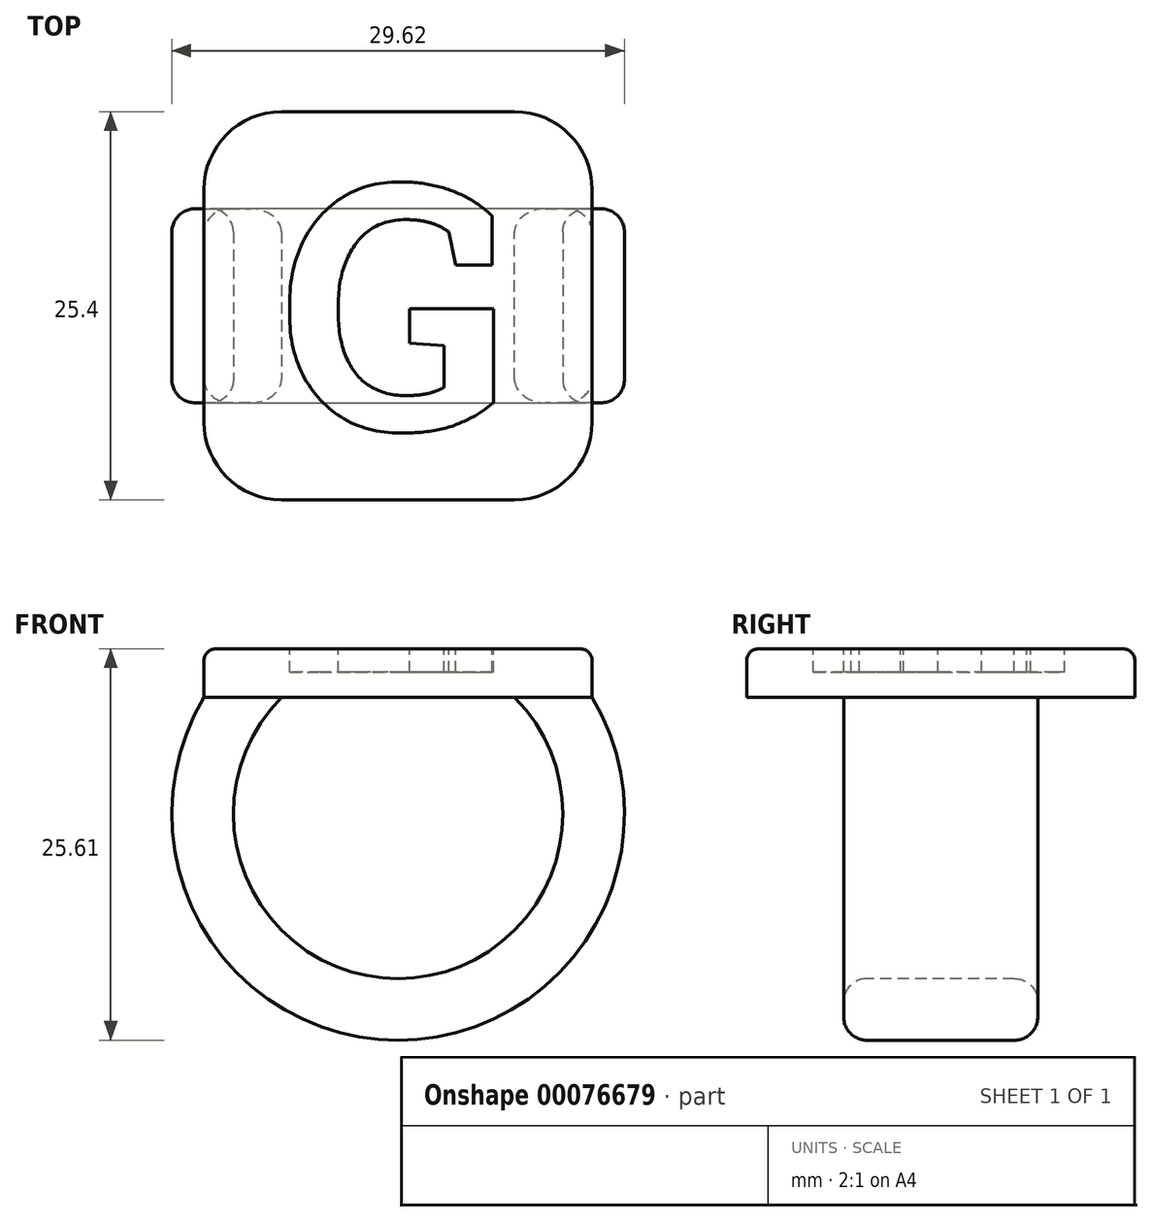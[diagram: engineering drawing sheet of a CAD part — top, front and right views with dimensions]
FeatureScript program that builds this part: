
annotation { "Feature Type Name" : "Feature", "Feature Type Description" : "" }
export const myFeature = defineFeature(function(context is Context, id is Id, definition is map)
    precondition{}
    {
        {
            var Q0;
            Q0=qCreatedBy(makeId("Top.planeOp"),FACE);
            var sketch = newSketch(context, id + "F0", { "sketchPlane" : qUnion([Q0])});
            skLineSegment(sketch, "E0.bottom", {"start": v(12.7, -12.7) * mm, "end": v(-12.7, -12.7) * mm});
            skLineSegment(sketch, "E0.top", {"start": v(12.7, 12.7) * mm, "end": v(-12.7, 12.7) * mm});
            skLineSegment(sketch, "E0.left", {"start": v(12.7, -12.7) * mm, "end": v(12.7, 12.7) * mm});
            skLineSegment(sketch, "E0.right", {"start": v(-12.7, -12.7) * mm, "end": v(-12.7, 12.7) * mm});
            skPoint(sketch, "E0.middle", {"position": v(0, 0) * mm});
            skSolve(sketch);
        }
        {
            var Q0;
            Q0 = qSketchRegion(id + "F0", true);
            extrude(context, id + "F1", {"entities" : qUnion([Q0]), "depth" : 3.17 * mm});
        }
        {
            var Q0;
            Q0=qCreatedBy(makeId("Front.planeOp"),FACE);
            var sketch = newSketch(context, id + "F2", { "sketchPlane" : qUnion([Q0])});
            skArc(sketch, "E1", {"start": v(-10.16, 0) * mm, "mid": v(0, -20.32) * mm, "end": v(10.16, 0) * mm});
            skSolve(sketch);
        }
        {
            var Q0;
            Q0=makeQuery(id+"F1.opExtrude","CAP_FACE",FACE,{"disambiguationData":[OSD([sQuery(id+"F0.wireOp",EDGE,"E0.bottom"),sQuery(id+"F0.wireOp",EDGE,"E0.top"),sQuery(id+"F0.wireOp",EDGE,"E0.left"),sQuery(id+"F0.wireOp",EDGE,"E0.right")])],"isStart":true});
            var sketch = newSketch(context, id + "F3", { "sketchPlane" : qUnion([Q0])});
            skLineSegment(sketch, "E2.bottom", {"start": v(-7.62, -6.35) * mm, "end": v(-12.7, -6.35) * mm});
            skLineSegment(sketch, "E2.top", {"start": v(-7.62, 6.35) * mm, "end": v(-12.7, 6.35) * mm});
            skLineSegment(sketch, "E2.left", {"start": v(-7.62, -6.35) * mm, "end": v(-7.62, 6.35) * mm});
            skLineSegment(sketch, "E2.right", {"start": v(-12.7, -6.35) * mm, "end": v(-12.7, 6.35) * mm});
            skPoint(sketch, "E2.middle", {"position": v(-10.16, 0) * mm});
            skSolve(sketch);
        }
        {
            var Q0;
            Q0 = qSketchRegion(id + "F3", true);
            var Q1;
            Q1 = qConstructionFilter(qBodyType(qCreatedBy(id + "F2" ,EDGE), BodyType.WIRE), ConstructionObject.NO);
            sweep(context, id + "F4", {"operationType" : NewBodyOperationType.ADD, "profiles" : qUnion([Q0]), "path" : qUnion([Q1])});
        }
        {
            var Q0;
            Q0=qCreatedBy(makeId("Front.planeOp"),FACE);
            var sketch = newSketch(context, id + "F5", { "sketchPlane" : qUnion([Q0])});
            skArc(sketch, "E3.0", {"start": v(9.45, -2.44) * mm, "mid": v(8.62, -1.15) * mm, "end": v(7.62, 0) * mm});
            skLineSegment(sketch, "E3.1", {"start": v(9.45, -2.44) * mm, "end": v(10.16, 0) * mm});
            skLineSegment(sketch, "E3.2", {"start": v(12.7, 0) * mm, "end": v(7.62, 0) * mm});
            skPoint(sketch, "E4.orphan", {"position": v(-7.62, 0) * mm});
            skLineSegment(sketch, "E5.trimOffspring", {"start": v(-7.62, 0) * mm, "end": v(-12.7, 0) * mm});
            skSolve(sketch);
        }
        {
            var Q0;
            Q0 = qSketchRegion(id + "F5", true);
            extrude(context, id + "F6", {"entities" : qUnion([Q0]), "operationType" : NewBodyOperationType.ADD, "depth" : 6.35 * mm, "hasSecondDirection" : true, "secondDirectionOppositeDirection" : true, "secondDirectionDepth" : 6.35 * mm});
        }
        {
            var Q0;
            Q0=makeQuery(id+"F1.opExtrude","SWEPT_EDGE",EDGE,{"disambiguationData":[OSD([sQuery(id+"F0.wireOp",EDGE,"E0.bottom"),sQuery(id+"F0.wireOp",EDGE,"E0.left")])]});
            var Q1;
            Q1=makeQuery(id+"F1.opExtrude","SWEPT_EDGE",EDGE,{"disambiguationData":[OSD([sQuery(id+"F0.wireOp",EDGE,"E0.top"),sQuery(id+"F0.wireOp",EDGE,"E0.left")])]});
            var Q2;
            Q2=makeQuery(id+"F1.opExtrude","SWEPT_EDGE",EDGE,{"disambiguationData":[OSD([sQuery(id+"F0.wireOp",EDGE,"E0.top"),sQuery(id+"F0.wireOp",EDGE,"E0.right")])]});
            var Q3;
            Q3=makeQuery(id+"F1.opExtrude","SWEPT_EDGE",EDGE,{"disambiguationData":[OSD([sQuery(id+"F0.wireOp",EDGE,"E0.bottom"),sQuery(id+"F0.wireOp",EDGE,"E0.right")])]});
            fillet(context, id + "F7", {"entities" : qUnion([Q0, Q1, Q2, Q3]), "radius" : 5.08 * mm, "tangentPropagation" : true, "allowEdgeOverflow" : false});
        }
        {
            var Q0;
            Q0=makeQuery(id+"F6.boolean.opBoolean","MERGE",EDGE,{"derivedFrom":[makeQuery(id+"F4.opSweep","SWEPT_EDGE",EDGE,{"disambiguationData":[OSD([sQuery(id+"F2.wireOp",EDGE,"E1"),sQuery(id+"F3.wireOp",EDGE,"E2.top"),sQuery(id+"F3.wireOp",EDGE,"E2.left")])]}),makeQuery(id+"F6.opExtrude","CAP_EDGE",EDGE,{"disambiguationData":[OSD([sQuery(id+"F5.wireOp",EDGE,"E3.0")])],"isStart":false})]});
            var Q1;
            Q1=makeQuery(id+"F4.opSweep","SWEPT_EDGE",EDGE,{"disambiguationData":[OSD([sQuery(id+"F0.wireOp",EDGE,"E0.right"),sQuery(id+"F2.wireOp",EDGE,"E1"),sQuery(id+"F3.wireOp",EDGE,"E2.top"),sQuery(id+"F3.wireOp",EDGE,"E2.right")])]});
            var Q2;
            Q2=makeQuery(id+"F4.opSweep","SWEPT_EDGE",EDGE,{"disambiguationData":[OSD([sQuery(id+"F0.wireOp",EDGE,"E0.right"),sQuery(id+"F2.wireOp",EDGE,"E1"),sQuery(id+"F3.wireOp",EDGE,"E2.bottom"),sQuery(id+"F3.wireOp",EDGE,"E2.right")])]});
            var Q3;
            Q3=makeQuery(id+"F6.boolean.opBoolean","MERGE",EDGE,{"derivedFrom":[makeQuery(id+"F4.opSweep","SWEPT_EDGE",EDGE,{"disambiguationData":[OSD([sQuery(id+"F2.wireOp",EDGE,"E1"),sQuery(id+"F3.wireOp",EDGE,"E2.bottom"),sQuery(id+"F3.wireOp",EDGE,"E2.left")])]}),makeQuery(id+"F6.opExtrude","CAP_EDGE",EDGE,{"disambiguationData":[OSD([sQuery(id+"F5.wireOp",EDGE,"E3.0")])],"isStart":true})]});
            fillet(context, id + "F8", {"entities" : qUnion([Q0, Q1, Q2, Q3]), "radius" : 1.52 * mm, "tangentPropagation" : true, "allowEdgeOverflow" : false});
        }
        {
            var Q0;
            Q0=makeQuery(id+"F1.opExtrude","CAP_EDGE",EDGE,{"disambiguationData":[OSD([sQuery(id+"F0.wireOp",EDGE,"E0.bottom")])],"isStart":false});
            fillet(context, id + "F9", {"entities" : qUnion([Q0]), "radius" : 0.76 * mm, "tangentPropagation" : true, "allowEdgeOverflow" : false});
        }
        {
            var Q0;
            Q0=makeQuery(id+"F1.opExtrude","CAP_FACE",FACE,{"disambiguationData":[OSD([sQuery(id+"F0.wireOp",EDGE,"E0.bottom"),sQuery(id+"F0.wireOp",EDGE,"E0.top"),sQuery(id+"F0.wireOp",EDGE,"E0.left"),sQuery(id+"F0.wireOp",EDGE,"E0.right")])],"isStart":false});
            var sketch = newSketch(context, id + "F10", { "sketchPlane" : qUnion([Q0])});
            skText(sketch, "E6", { "text": "G\n", "fontName": "RobotoSlab-Bold.ttf"});
            skLineSegment(sketch, "E7", {"start": v(-7.62, 0) * mm, "end": v(7.62, 0) * mm, "construction": true});
            skPoint(sketch, "E8", {"position": v(0, 0) * mm});
            const initialGuessF10  = {"E6": [-0.00762, -0.0081, 1, 0, 0.01618]};
            skSetInitialGuess(sketch, initialGuessF10);
            skSolve(sketch);
        }
        {
            var Q0;
            Q0 = qSketchRegion(id + "F10", true);
            extrude(context, id + "F11", {"entities" : qUnion([Q0]), "operationType" : NewBodyOperationType.REMOVE, "oppositeDirection" : true, "depth" : 1.52 * mm});
        }
    });
